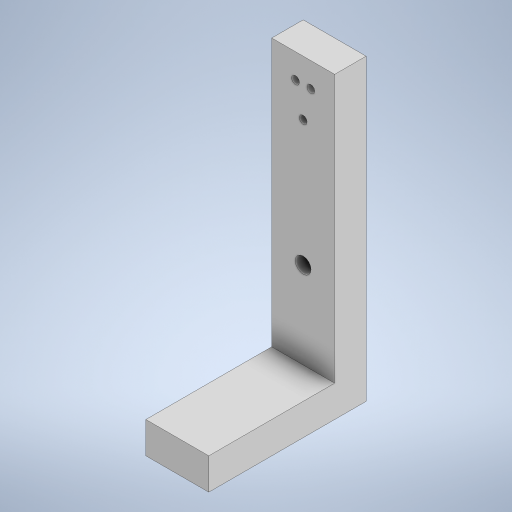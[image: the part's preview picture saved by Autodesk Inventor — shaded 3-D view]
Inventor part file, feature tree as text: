
AUTODESK INVENTOR PART (.ipt)
format: ipt  version: 2023 (Build 270158000, 158)  size: 251,904 bytes
history: native  units: in
note: dims shown in document units (in); Inventor stores cm internally (conversion verified against a paired STEP export)
features: extrude x2, sketch x2
ambient origin geometry x8: Origin, YZ Plane, XZ Plane, XY Plane, X Axis, Y Axis, Z Axis, Center Point
bodies: Solid1 (feature_tree)
feature tree (4):
  extrude  "Extrusion1"  Depth=0.5in
  extrude  "Extrusion2"  Depth=2.5in
  sketch  "Sketch1"  dims[d0=4.25in d1=0.5in]
  sketch  "Sketch2"  dims[d2=4.75in d3=2.5in d4=1.0in d5=0.0in d7=0.25in d8=0.125in d9=1.375in d10=2.0in d11=0.125in d12=0.5in d17=0.125in d18=0.5in d20=1.0in d21=0.0in d22=0.1213in d23=0.1213in]
